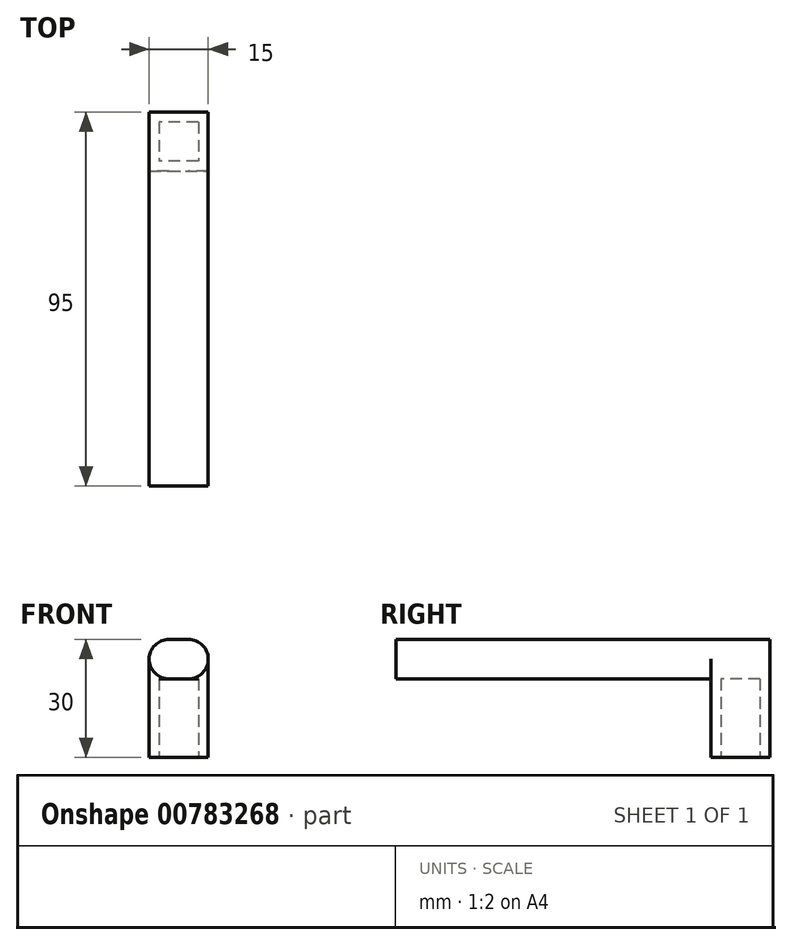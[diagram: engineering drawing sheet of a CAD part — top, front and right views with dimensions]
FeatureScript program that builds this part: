
annotation { "Feature Type Name" : "Feature", "Feature Type Description" : "" }
export const myFeature = defineFeature(function(context is Context, id is Id, definition is map)
    precondition{}
    {
        {
            var Q0;
            Q0=qCreatedBy(makeId("Top.planeOp"),FACE);
            var sketch = newSketch(context, id + "F0", { "sketchPlane" : qUnion([Q0])});
            skLineSegment(sketch, "E0.bottom", {"start": v(-7.5, 7.5) * mm, "end": v(7.5, 7.5) * mm});
            skLineSegment(sketch, "E0.top", {"start": v(-7.5, -7.5) * mm, "end": v(7.5, -7.5) * mm});
            skLineSegment(sketch, "E0.left", {"start": v(-7.5, 7.5) * mm, "end": v(-7.5, -7.5) * mm});
            skLineSegment(sketch, "E0.right", {"start": v(7.5, 7.5) * mm, "end": v(7.5, -7.5) * mm});
            skPoint(sketch, "E0.middle", {"position": v(0, 0) * mm});
            skSolve(sketch);
        }
        {
            var Q0;
            Q0 = qSketchRegion(id + "F0", true);
            extrude(context, id + "F1", {"entities" : qUnion([Q0]), "depth" : 30 * mm, "offsetDistance" : 25.4 * mm});
        }
        {
            var Q0;
            Q0=makeQuery(id+"F1.opExtrude","SWEPT_FACE",FACE,{"disambiguationData":[OSD([sQuery(id+"F0.wireOp",EDGE,"E0.top")])]});
            var sketch = newSketch(context, id + "F2", { "sketchPlane" : qUnion([Q0])});
            skLineSegment(sketch, "E1.bottom", {"start": v(-7.5, 30) * mm, "end": v(7.5, 30) * mm});
            skLineSegment(sketch, "E1.top", {"start": v(-7.5, 20) * mm, "end": v(7.5, 20) * mm});
            skLineSegment(sketch, "E1.left", {"start": v(-7.5, 30) * mm, "end": v(-7.5, 20) * mm});
            skLineSegment(sketch, "E1.right", {"start": v(7.5, 30) * mm, "end": v(7.5, 20) * mm});
            skSolve(sketch);
        }
        {
            var Q0;
            Q0 = qSketchRegion(id + "F2", true);
            extrude(context, id + "F3", {"entities" : qUnion([Q0]), "operationType" : NewBodyOperationType.ADD, "depth" : 80 * mm, "offsetDistance" : 25.4 * mm});
        }
        {
            var Q0;
            Q0=makeQuery(id+"F3.boolean.opBoolean","MERGE",EDGE,{"derivedFrom":[makeQuery(id+"F1.opExtrude","CAP_EDGE",EDGE,{"disambiguationData":[OSD([sQuery(id+"F0.wireOp",EDGE,"E0.right")])],"isStart":false}),makeQuery(id+"F3.opExtrude","SWEPT_EDGE",EDGE,{"disambiguationData":[OSD([sQuery(id+"F2.wireOp",EDGE,"yLJVQLuw-PsVT-kJuG-LmH2-xaGAANeYKveH.bottom"),sQuery(id+"F2.wireOp",EDGE,"yLJVQLuw-PsVT-kJuG-LmH2-xaGAANeYKveH.right")])]})]});
            var Q1;
            Q1=makeQuery(id+"F3.boolean.opBoolean","MERGE",EDGE,{"derivedFrom":[makeQuery(id+"F1.opExtrude","CAP_EDGE",EDGE,{"disambiguationData":[OSD([sQuery(id+"F0.wireOp",EDGE,"E0.left")])],"isStart":false}),makeQuery(id+"F3.opExtrude","SWEPT_EDGE",EDGE,{"disambiguationData":[OSD([sQuery(id+"F2.wireOp",EDGE,"yLJVQLuw-PsVT-kJuG-LmH2-xaGAANeYKveH.bottom"),sQuery(id+"F2.wireOp",EDGE,"yLJVQLuw-PsVT-kJuG-LmH2-xaGAANeYKveH.left")])]})]});
            var Q2;
            Q2=makeQuery(id+"F3.opExtrude","SWEPT_EDGE",EDGE,{"disambiguationData":[OSD([sQuery(id+"F0.wireOp",EDGE,"E0.top"),sQuery(id+"F0.wireOp",EDGE,"E0.right"),sQuery(id+"F2.wireOp",EDGE,"yLJVQLuw-PsVT-kJuG-LmH2-xaGAANeYKveH.top"),sQuery(id+"F2.wireOp",EDGE,"yLJVQLuw-PsVT-kJuG-LmH2-xaGAANeYKveH.right")])]});
            var Q3;
            Q3=makeQuery(id+"F3.opExtrude","SWEPT_EDGE",EDGE,{"disambiguationData":[OSD([sQuery(id+"F0.wireOp",EDGE,"E0.top"),sQuery(id+"F0.wireOp",EDGE,"E0.left"),sQuery(id+"F2.wireOp",EDGE,"yLJVQLuw-PsVT-kJuG-LmH2-xaGAANeYKveH.top"),sQuery(id+"F2.wireOp",EDGE,"yLJVQLuw-PsVT-kJuG-LmH2-xaGAANeYKveH.left")])]});
            fillet(context, id + "F4", {"entities" : qUnion([Q0, Q1, Q2, Q3]), "radius" : 5 * mm, "tangentPropagation" : true, "allowEdgeOverflow" : false});
        }
        {
            var Q0;
            Q0=makeQuery(id+"F1.opExtrude","CAP_FACE",FACE,{"disambiguationData":[OSD([sQuery(id+"F0.wireOp",EDGE,"E0.bottom"),sQuery(id+"F0.wireOp",EDGE,"E0.top"),sQuery(id+"F0.wireOp",EDGE,"E0.left"),sQuery(id+"F0.wireOp",EDGE,"E0.right")])],"isStart":true});
            var sketch = newSketch(context, id + "F5", { "sketchPlane" : qUnion([Q0])});
            skLineSegment(sketch, "E2.bottom", {"start": v(5, -5) * mm, "end": v(-5, -5) * mm});
            skLineSegment(sketch, "E2.top", {"start": v(5, 5) * mm, "end": v(-5, 5) * mm});
            skLineSegment(sketch, "E2.left", {"start": v(5, -5) * mm, "end": v(5, 5) * mm});
            skLineSegment(sketch, "E2.right", {"start": v(-5, -5) * mm, "end": v(-5, 5) * mm});
            skPoint(sketch, "E2.middle", {"position": v(0, 0) * mm});
            skSolve(sketch);
        }
        {
            var Q0;
            Q0 = qSketchRegion(id + "F5", true);
            extrude(context, id + "F6", {"entities" : qUnion([Q0]), "operationType" : NewBodyOperationType.REMOVE, "oppositeDirection" : true, "depth" : 20 * mm, "offsetDistance" : 25.4 * mm});
        }
    });
